# Revit family: BuroSeating_Polo Stool
name_source: partatom
category: Furniture
units: mm (PartAtom-declared; Revit-internal decimal feet)

## family parameters
Always vertical = Yes
Cut with Voids When Loaded = No
OmniClass Number = 23.40.70.14.64.11
OmniClass Title = Office Furniture
Room Calculation Point = No
Shared = No
Work Plane-Based = No

## types (2) — shared parameters
Assembly Code = E2020
BottomLiftMaterial = BuroSeating_Aluminium_Black
CastorCoverMaterial = BuroSeating_Aluminium_Brushed_Black
CastorMaterial = BuroSeating_Aluminium_Black
CastorWheelMaterial = BuroSeating_Aluminium_Black
FeetMaterial = BuroSeating_Aluminium_Brushed_Black
FootRingMaterial = BuroSeating_Aluminium_Black
Manufacturer = Buro Seating
NominalDepth = 580 mm  [stored 1.90289 ft]
NominalWidth = 580 mm  [stored 1.90289 ft]
ProductGroup = Polo
ProductPageURL AU = https://buroseating.com
ProductPageURL NZ = https://buroseating.co.nz
ProductRange = Buro
SeatDiameter = 385 mm  [stored 1.26312 ft]
SeatMaterial = BuroSeating_Leather_Black
SeatTiltMaterial = BuroSeating_Aluminium_Black
TopLiftMaterial = BuroSeating_Aluminium_Black
Type Comments = Seat Height 615-860mm High
URL = https://buroseating.co.nz
URL AU = https://buroseating.com
WarrantyDescription = Full 5 year guarantee (excluding upholstery)
zero-valued in all types: Default Elevation

## per-type parameters (varying)
| type | Description | Footring | Model | NominalSeatHeight |
| Buro Polo Stool w Footring | Buro Polo Stool with Footring | Yes | 142-PU3-AT | 615-860h |
| Buro Polo Stool | Buro Polo Stool | No |  | 460-560h |

note: [stored X ft] marks values corroborated as IEEE doubles in the binary element streams (Revit-internal decimal feet)

## geometry (parser evidence)
native form markers: Sweep x5
no freeform markers — native parametric forms only
